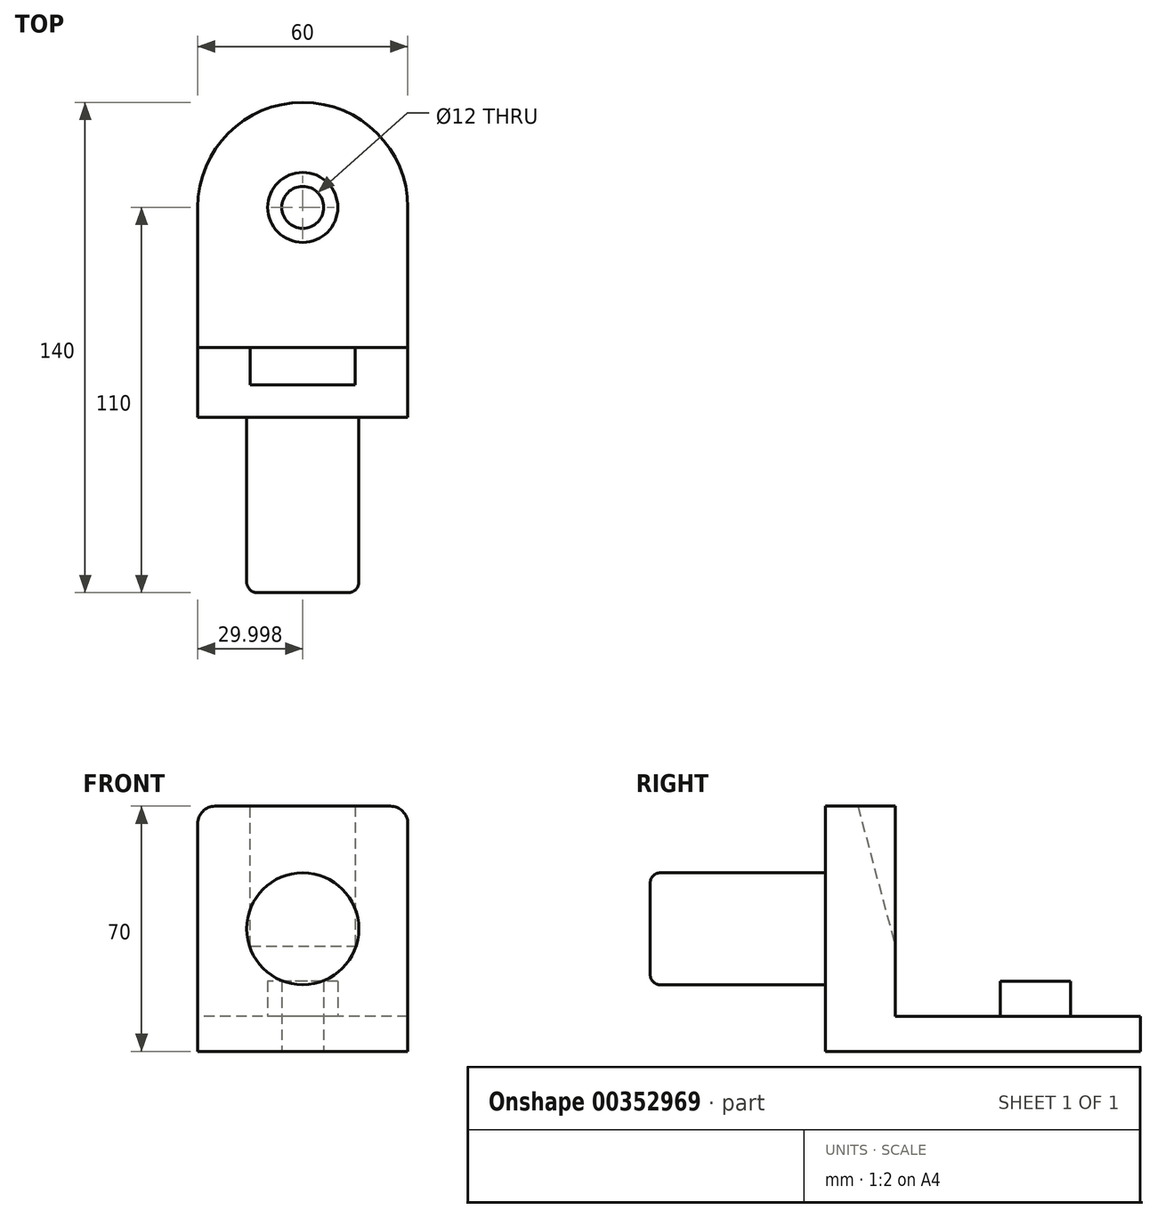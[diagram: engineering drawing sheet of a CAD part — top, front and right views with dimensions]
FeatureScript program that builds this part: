
annotation { "Feature Type Name" : "Feature", "Feature Type Description" : "" }
export const myFeature = defineFeature(function(context is Context, id is Id, definition is map)
    precondition{}
    {
        {
            var Q0;
            Q0=qCreatedBy(makeId("Top.planeOp"),FACE);
            var sketch = newSketch(context, id + "F0", { "sketchPlane" : qUnion([Q0])});
            skLineSegment(sketch, "E0", {"start": v(-34.85, 0) * mm, "end": v(-34.85, 40) * mm});
            skLineSegment(sketch, "E1", {"start": v(-4.85, 70) * mm, "end": v(-4.85, 70) * mm});
            skLineSegment(sketch, "E2", {"start": v(25.15, 40) * mm, "end": v(25.15, 0) * mm});
            skLineSegment(sketch, "E3", {"start": v(25.15, 0) * mm, "end": v(25.15, -20) * mm});
            skLineSegment(sketch, "E4", {"start": v(25.15, -20) * mm, "end": v(-34.85, -20) * mm});
            skLineSegment(sketch, "E5", {"start": v(-34.85, -20) * mm, "end": v(-34.85, 0) * mm});
            skLineSegment(sketch, "E6", {"start": v(25.15, 0) * mm, "end": v(-34.85, 0) * mm});
            skPoint(sketch, "E7.visualSharp", {"position": v(-34.85, 70) * mm});
            skArc(sketch, "E7.filletArc", {"start": v(-4.85, 70) * mm, "mid": v(-26.07, 61.21) * mm, "end": v(-34.85, 40) * mm});
            skPoint(sketch, "E8.visualSharp", {"position": v(25.15, 70) * mm});
            skArc(sketch, "E8.filletArc", {"start": v(25.15, 40) * mm, "mid": v(16.36, 61.21) * mm, "end": v(-4.85, 70) * mm});
            skCircle(sketch, "E9", {"center": v(-4.85, 40) * mm, "radius": 10 * mm});
            skCircle(sketch, "E10", {"center": v(-4.85, 40) * mm, "radius": 6 * mm});
            skSolve(sketch);
        }
        {
            var Q0;
            Q0=makeQuery(id+"F0.imprint","IMPRINT",FACE,{"disambiguationData":[TD([[makeQuery(id+"F0.imprint","IMPRINT",EDGE,{"derivedFrom":sQuery(id+"F0.wireOp",EDGE,"E0")}),-1.0]])]});
            extrude(context, id + "F1", {"entities" : qUnion([Q0]), "depth" : 10 * mm});
        }
        {
            var Q0;
            Q0=makeQuery(id+"F0.imprint","IMPRINT",FACE,{"disambiguationData":[TD([[makeQuery(id+"F0.imprint","IMPRINT",EDGE,{"derivedFrom":sQuery(id+"F0.wireOp",EDGE,"E9")}),1.0]])]});
            extrude(context, id + "F2", {"entities" : qUnion([Q0]), "operationType" : NewBodyOperationType.ADD, "depth" : 20 * mm});
        }
        {
            var Q0;
            Q0=makeQuery(id+"F0.imprint","IMPRINT",FACE,{"disambiguationData":[TD([[makeQuery(id+"F0.imprint","IMPRINT",EDGE,{"derivedFrom":sQuery(id+"F0.wireOp",EDGE,"E3")}),-1.0]])]});
            extrude(context, id + "F3", {"entities" : qUnion([Q0]), "operationType" : NewBodyOperationType.ADD, "depth" : 70 * mm});
        }
        {
            var Q0;
            Q0=makeQuery(id+"F3.opExtrude","SWEPT_FACE",FACE,{"disambiguationData":[OSD([sQuery(id+"F0.wireOp",EDGE,"E4")])]});
            var sketch = newSketch(context, id + "F4", { "sketchPlane" : qUnion([Q0])});
            skCircle(sketch, "E11", {"center": v(-4.85, 35) * mm, "radius": 16 * mm});
            skPoint(sketch, "E12.orphan", {"position": v(-34.85, 27.42) * mm});
            skPoint(sketch, "E13.orphan", {"position": v(-4.85, 0) * mm});
            skPoint(sketch, "E14.orphan", {"position": v(-4.85, 27.42) * mm});
            skPoint(sketch, "E15.end.orphan", {"position": v(25.15, 27.42) * mm});
            skSolve(sketch);
        }
        {
            var Q0;
            Q0=makeQuery(id+"F4.imprint","IMPRINT",FACE,{"disambiguationData":[TD([[makeQuery(id+"F4.imprint","IMPRINT",EDGE,{"derivedFrom":sQuery(id+"F4.wireOp",EDGE,"E11")}),1.0]])]});
            extrude(context, id + "F5", {"entities" : qUnion([Q0]), "operationType" : NewBodyOperationType.ADD, "depth" : 50 * mm});
        }
        {
            var Q0;
            Q0=makeQuery(id+"F5.opExtrude","CAP_EDGE",EDGE,{"disambiguationData":[OSD([sQuery(id+"F4.wireOp",EDGE,"E11")])],"isStart":false});
            fillet(context, id + "F6", {"entities" : qUnion([Q0]), "radius" : 3 * mm, "tangentPropagation" : true, "allowEdgeOverflow" : false});
        }
        {
            var Q0;
            Q0=makeQuery(id+"F3.boolean.opBoolean","MERGE",FACE,{"derivedFrom":[makeQuery(id+"F1.opExtrude","SWEPT_FACE",FACE,{"disambiguationData":[OSD([sQuery(id+"F0.wireOp",EDGE,"E2")])]}),makeQuery(id+"F3.opExtrude","SWEPT_FACE",FACE,{"disambiguationData":[OSD([sQuery(id+"F0.wireOp",EDGE,"E3")])]})]});
            var sketch = newSketch(context, id + "F7", { "sketchPlane" : qUnion([Q0])});
            skLineSegment(sketch, "E16", {"start": v(0, 70) * mm, "end": v(0, 30) * mm});
            skLineSegment(sketch, "E17", {"start": v(0, 30) * mm, "end": v(-10.72, 70) * mm});
            skLineSegment(sketch, "E18", {"start": v(-10.72, 70) * mm, "end": v(0, 70) * mm});
            skSolve(sketch);
        }
        {
            var Q0;
            Q0=makeQuery(id+"F3.boolean.opBoolean","MERGE",FACE,{"derivedFrom":[makeQuery(id+"F1.opExtrude","SWEPT_FACE",FACE,{"disambiguationData":[OSD([sQuery(id+"F0.wireOp",EDGE,"E0")])]}),makeQuery(id+"F3.opExtrude","SWEPT_FACE",FACE,{"disambiguationData":[OSD([sQuery(id+"F0.wireOp",EDGE,"E5")])]})]});
            var sketch = newSketch(context, id + "F8", { "sketchPlane" : qUnion([Q0])});
            skLineSegment(sketch, "E19", {"start": v(0, 70) * mm, "end": v(0, 30) * mm});
            skLineSegment(sketch, "E20", {"start": v(0, 30) * mm, "end": v(10.72, 70) * mm});
            skSolve(sketch);
        }
        {
            var Q0;
            Q0=makeQuery(id+"F7.imprint","IMPRINT",FACE,{"disambiguationData":[TD([[makeQuery(id+"F7.imprint","IMPRINT",EDGE,{"derivedFrom":sQuery(id+"F7.wireOp",EDGE,"E16")}),-1.0]])]});
            extrude(context, id + "F9", {"entities" : qUnion([Q0]), "operationType" : NewBodyOperationType.REMOVE, "oppositeDirection" : true, "depth" : 65.1 * mm});
        }
        {
            var Q0;
            {var subQ4=sQuery(id+"F8.wireOp",EDGE,"E20");Q0=makeQuery(id+"F8.imprint","IMPRINT",FACE,{"disambiguationData":[TD([[makeQuery(id+"F8.imprint","IMPRINT",EDGE,{"derivedFrom":subQ4}),-1.0]])]});}
            var Q1;
            {var subQ0=sQuery(id+"F8.wireOp",EDGE,"E19");Q1=makeQuery(id+"F8.imprint","IMPRINT",FACE,{"disambiguationData":[TD([[makeQuery(id+"F8.imprint","IMPRINT",EDGE,{"derivedFrom":subQ0}),1.0]])]});}
            extrude(context, id + "F10", {"entities" : qUnion([Q0, Q1]), "operationType" : NewBodyOperationType.ADD, "oppositeDirection" : true, "depth" : 15 * mm});
        }
        {
            var Q0;
            {var subQ4=sQuery(id+"F7.wireOp",EDGE,"E17");Q0=makeQuery(id+"F7.imprint","IMPRINT",FACE,{"disambiguationData":[TD([[makeQuery(id+"F7.imprint","IMPRINT",EDGE,{"derivedFrom":subQ4}),1.0]])]});}
            var Q1;
            Q1=makeQuery(id+"F7.imprint","IMPRINT",FACE,{"disambiguationData":[TD([[makeQuery(id+"F7.imprint","IMPRINT",EDGE,{"derivedFrom":sQuery(id+"F7.wireOp",EDGE,"E16")}),-1.0]])]});
            extrude(context, id + "F11", {"entities" : qUnion([Q0, Q1]), "operationType" : NewBodyOperationType.ADD, "oppositeDirection" : true, "depth" : 15 * mm});
        }
        {
            var Q0;
            {var subQ0=sQuery(id+"F0.wireOp",EDGE,"E5");Q0=makeQuery(id+"F10.boolean.opBoolean","MERGE",EDGE,{"derivedFrom":[makeQuery(id+"F3.opExtrude","CAP_EDGE",EDGE,{"disambiguationData":[OSD([subQ0])],"isStart":false}),makeQuery(id+"F10.opExtrude","CAP_EDGE",EDGE,{"disambiguationData":[OSD([subQ0])],"isStart":true})]});}
            fillet(context, id + "F12", {"entities" : qUnion([Q0]), "radius" : 5 * mm, "tangentPropagation" : true, "allowEdgeOverflow" : false});
        }
        {
            var Q0;
            {var subQ0=sQuery(id+"F0.wireOp",EDGE,"E3");Q0=makeQuery(id+"F11.boolean.opBoolean","MERGE",EDGE,{"derivedFrom":[makeQuery(id+"F3.opExtrude","CAP_EDGE",EDGE,{"disambiguationData":[OSD([subQ0])],"isStart":false}),makeQuery(id+"F11.opExtrude","CAP_EDGE",EDGE,{"disambiguationData":[OSD([subQ0,sQuery(id+"F7.wireOp",EDGE,"E18")])],"isStart":true})]});}
            fillet(context, id + "F13", {"entities" : qUnion([Q0]), "radius" : 5 * mm, "tangentPropagation" : true, "allowEdgeOverflow" : false});
        }
    });
